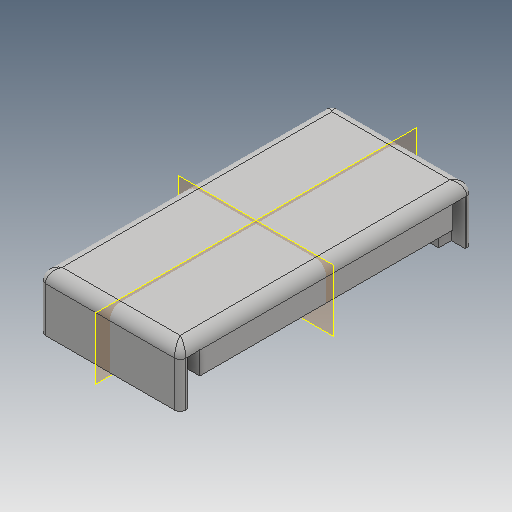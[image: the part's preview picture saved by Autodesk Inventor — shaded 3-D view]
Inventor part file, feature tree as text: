
AUTODESK INVENTOR PART (.ipt)
format: ipt  version: 2019 (Build 230136000, 136)  size: 225,280 bytes
history: native  units: mm
features: reference x7, projected_geometry x6, extrude x4, sketch x4, mirror x3, fillet x3, plane x2
ambient origin geometry x8: Origin, YZ Plane, XZ Plane, XY Plane, X Axis, Y Axis, Z Axis, Center Point
bodies: Solid1 (feature_tree)
feature tree (29):
  extrude  "Extrusion1"  Depth=3.0mm TaperAngle=0.0deg
  extrude  "Extrusion2"  Depth=3.5mm TaperAngle=0.0deg
  extrude  "Extrusion3"  Depth=1.25mm
  plane  "Work Plane1"
  plane  "Work Plane2"
  mirror  "Mirror1"
  mirror  "Mirror2"
  extrude  "Extrusion4"  Depth=1.0mm
  mirror  "Mirror3"
  fillet  "Fillet1"  Radius=3.5mm
  fillet  "Fillet3"  Radius=1.0mm
  fillet  "Fillet4"  Radius=1.0mm
  sketch  "Sketch1"  dims[d0=26.0mm d1=3.0mm d2=0.0mm]
  reference  "Reference1"
  reference  "Reference2"
  sketch  "Sketch2"  dims[d3=2.0mm d4=0.0mm d17=3.5mm d18=0.0mm]
  projected_geometry  "Projected Loop1"
  reference  "Reference3"
  sketch  "Sketch4"  dims[d19=1.125mm d20=1.25mm]
  projected_geometry  "Projected Loop3"
  projected_geometry  "Projected Loop4"
  reference  "Reference4"
  reference  "Reference5"
  reference  "Reference6"
  reference  "Reference7"
  sketch  "Sketch5"  dims[d21=1.0mm d22=1.0mm d24=3.5mm d25=0.0mm d26=1.0mm d28=1.0mm d29=0.5mm]
  projected_geometry  "Projected Loop5"
  projected_geometry  "Projected Loop6"
  projected_geometry  "Projected Loop7"
